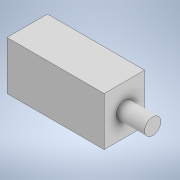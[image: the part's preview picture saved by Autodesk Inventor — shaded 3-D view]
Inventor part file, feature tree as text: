
AUTODESK INVENTOR PART (.ipt)
format: ipt  version: 2020 (Build 240168000, 168)  size: 102,912 bytes
history: native  units: mm
features: extrude x2, sketch x2
ambient origin geometry x8: Origin, YZ Plane, XZ Plane, XY Plane, X Axis, Y Axis, Z Axis, Center Point
bodies: Solid1 (feature_tree)
feature tree (4):
  extrude  "Extrusion1"  Depth=10.0mm
  extrude  "Extrusion2"  Depth=7.0mm
  sketch  "Sketch1"  dims[d0=24.0mm d1=10.0mm]
  sketch  "Sketch2"  dims[d2=12.0mm d3=0.0mm d4=4.0mm d5=7.0mm d6=0.0mm]
